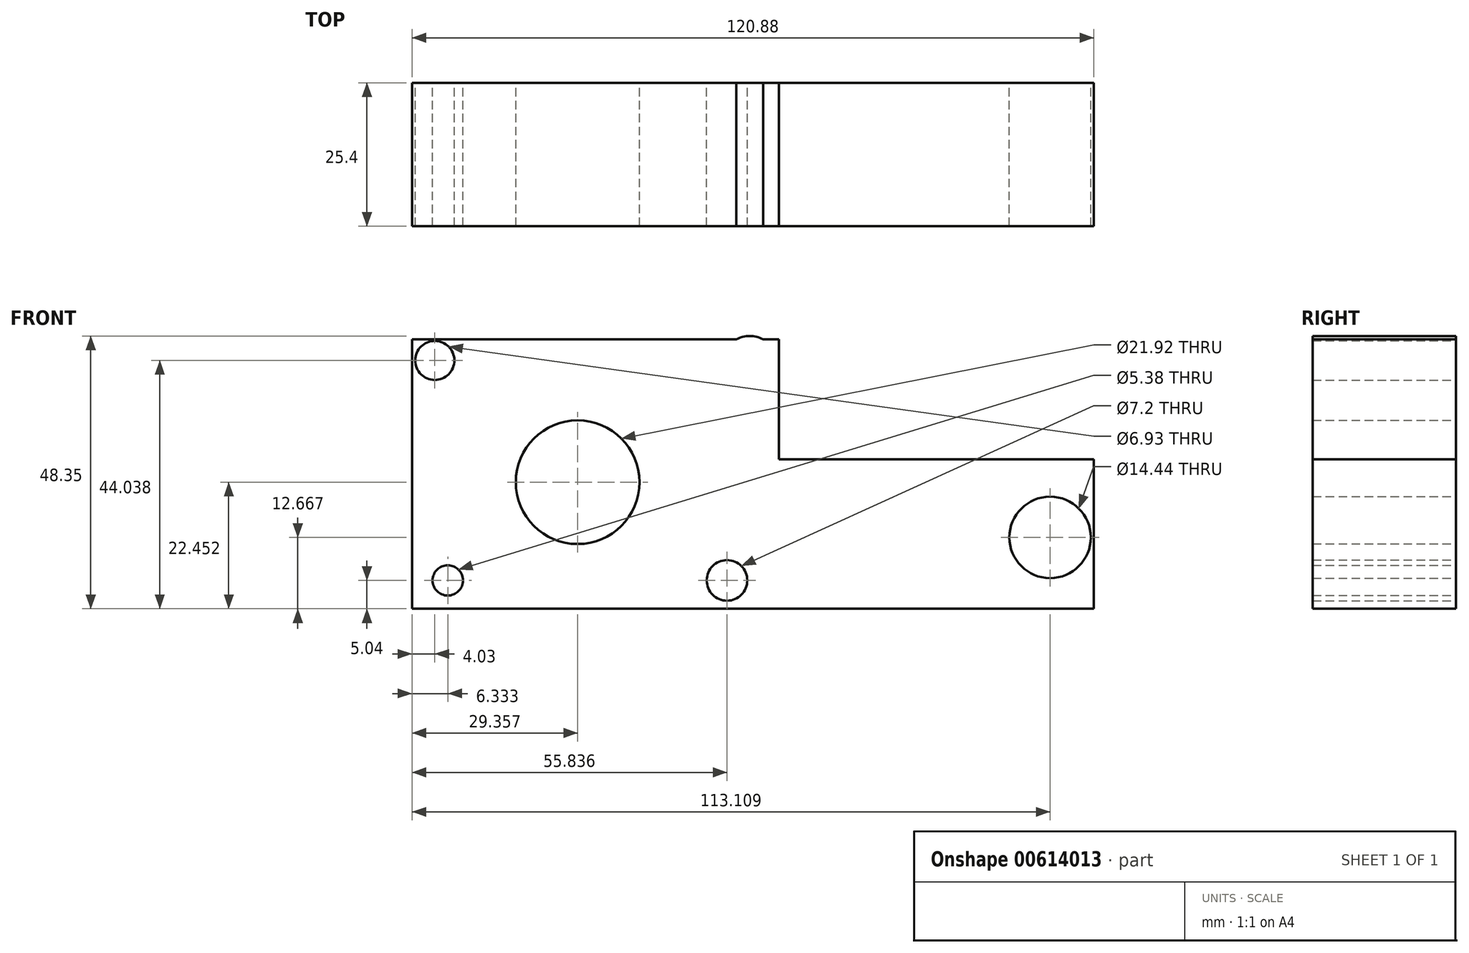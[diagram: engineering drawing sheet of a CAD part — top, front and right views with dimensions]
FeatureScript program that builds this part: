
annotation { "Feature Type Name" : "Feature", "Feature Type Description" : "" }
export const myFeature = defineFeature(function(context is Context, id is Id, definition is map)
    precondition{}
    {
        {
            var Q0;
            Q0=qCreatedBy(makeId("Front.planeOp"),FACE);
            var sketch = newSketch(context, id + "F0", { "sketchPlane" : qUnion([Q0])});
            skLineSegment(sketch, "E0", {"start": v(-72.96, 42.74) * mm, "end": v(-7.91, 42.74) * mm});
            skLineSegment(sketch, "E1", {"start": v(-7.91, 42.74) * mm, "end": v(-7.91, 21.44) * mm});
            skLineSegment(sketch, "E2", {"start": v(-7.91, 21.44) * mm, "end": v(47.92, 21.44) * mm});
            skLineSegment(sketch, "E3", {"start": v(47.92, 21.44) * mm, "end": v(47.92, -5.04) * mm});
            skLineSegment(sketch, "E4", {"start": v(47.92, -5.04) * mm, "end": v(-72.96, -5.04) * mm});
            skLineSegment(sketch, "E5", {"start": v(-72.96, -5.04) * mm, "end": v(-72.96, 42.74) * mm});
            skCircle(sketch, "E6", {"center": v(-68.93, 39) * mm, "radius": 3.47 * mm});
            skCircle(sketch, "E7", {"center": v(-13.1, 38.13) * mm, "radius": 5.18 * mm});
            skCircle(sketch, "E8", {"center": v(-17.12, 0) * mm, "radius": 3.6 * mm});
            skCircle(sketch, "E9", {"center": v(-66.63, 0) * mm, "radius": 2.69 * mm});
            skCircle(sketch, "E10", {"center": v(-43.6, 17.41) * mm, "radius": 10.96 * mm});
            skCircle(sketch, "E11", {"center": v(40.15, 7.63) * mm, "radius": 7.22 * mm});
            skSolve(sketch);
        }
        {
            var Q0;
            Q0 = qSketchRegion(id + "F0", true);
            extrude(context, id + "F1", {"entities" : qUnion([Q0]), "depth" : 25.4 * mm, "offsetDistance" : 25.4 * mm});
        }
    });
